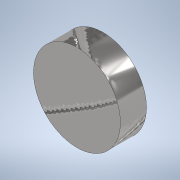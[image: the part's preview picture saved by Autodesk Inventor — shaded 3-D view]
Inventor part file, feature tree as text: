
AUTODESK INVENTOR PART (.ipt)
format: ipt  version: 2020 (Build 240168000, 168)  size: 98,304 bytes
history: native  units: mm
features: extrude x1, sketch x1
ambient origin geometry x8: Origin, YZ Plane, XZ Plane, XY Plane, X Axis, Y Axis, Z Axis, Center Point
bodies: Solid1 (feature_tree)
feature tree (2):
  extrude  "Extrusion1"  Depth=3.0mm TaperAngle=0.0deg
  sketch  "Sketch1"  dims[d0=10.0mm d1=3.0mm d2=0.0mm]
